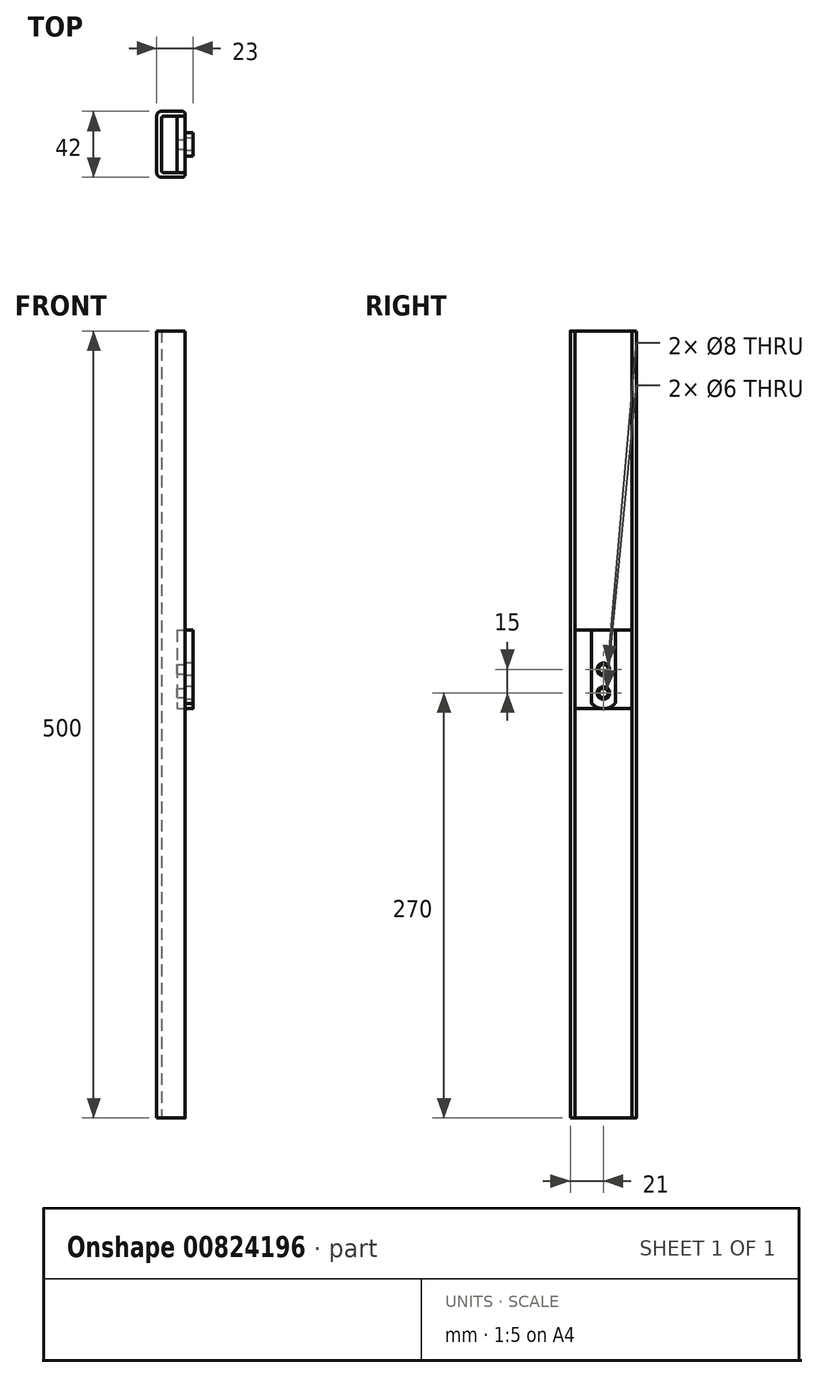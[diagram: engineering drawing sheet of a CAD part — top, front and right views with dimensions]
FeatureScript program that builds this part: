
annotation { "Feature Type Name" : "Feature", "Feature Type Description" : "" }
export const myFeature = defineFeature(function(context is Context, id is Id, definition is map)
    precondition{}
    {
        {
            var Q0;
            Q0=qCreatedBy(makeId("Top.planeOp"),FACE);
            var sketch = newSketch(context, id + "F0", { "sketchPlane" : qUnion([Q0])});
            skLineSegment(sketch, "E0.bottom", {"start": v(7, 21) * mm, "end": v(-6, 21) * mm});
            skLineSegment(sketch, "E0.top", {"start": v(7, -21) * mm, "end": v(-6, -21) * mm});
            skLineSegment(sketch, "E0.left", {"start": v(9, 19) * mm, "end": v(9, -19) * mm});
            skLineSegment(sketch, "E0.right", {"start": v(-9, 18) * mm, "end": v(-9, -18) * mm});
            skPoint(sketch, "E0.middle", {"position": v(0, 0) * mm});
            skLineSegment(sketch, "E1.0", {"start": v(9, -18) * mm, "end": v(-4.5, -18) * mm});
            skLineSegment(sketch, "E1.1", {"start": v(-6, 16.5) * mm, "end": v(-6, -16.5) * mm});
            skLineSegment(sketch, "E1.2", {"start": v(9, 18) * mm, "end": v(-4.5, 18) * mm});
            skPoint(sketch, "E2.visualSharp", {"position": v(-6, 18) * mm});
            skArc(sketch, "E2.filletArc", {"start": v(-4.5, 18) * mm, "mid": v(-5.56, 17.56) * mm, "end": v(-6, 16.5) * mm});
            skPoint(sketch, "E3.visualSharp", {"position": v(-6, -18) * mm});
            skArc(sketch, "E3.filletArc", {"start": v(-6, -16.5) * mm, "mid": v(-5.56, -17.56) * mm, "end": v(-4.5, -18) * mm});
            skPoint(sketch, "E4.visualSharp", {"position": v(-9, -21) * mm});
            skArc(sketch, "E4.filletArc", {"start": v(-9, -18) * mm, "mid": v(-8.12, -20.12) * mm, "end": v(-6, -21) * mm});
            skPoint(sketch, "E5.visualSharp", {"position": v(-9, 21) * mm});
            skArc(sketch, "E5.filletArc", {"start": v(-6, 21) * mm, "mid": v(-8.12, 20.12) * mm, "end": v(-9, 18) * mm});
            skPoint(sketch, "E6.visualSharp", {"position": v(9, -21) * mm});
            skArc(sketch, "E6.filletArc", {"start": v(7, -21) * mm, "mid": v(8.41, -20.41) * mm, "end": v(9, -19) * mm});
            skPoint(sketch, "E7.visualSharp", {"position": v(9, 21) * mm});
            skArc(sketch, "E7.filletArc", {"start": v(9, 19) * mm, "mid": v(8.41, 20.41) * mm, "end": v(7, 21) * mm});
            skSolve(sketch);
        }
        {
            var Q0;
            {var subQ2=sQuery(id+"F0.wireOp",EDGE,"E0.bottom");Q0=makeQuery(id+"F0.imprint","IMPRINT",FACE,{"disambiguationData":[TD([[makeQuery(id+"F0.imprint","IMPRINT",EDGE,{"derivedFrom":subQ2}),1.0]])]});}
            extrude(context, id + "F1", {"entities" : qUnion([Q0]), "depth" : 500 * mm, "offsetDistance" : 25 * mm});
        }
        {
            var Q0;
            {var subQ0=sQuery(id+"F0.wireOp",EDGE,"E0.left");Q0=makeQuery(id+"F1.opExtrude","SWEPT_FACE",FACE,{"disambiguationData":[OSD([subQ0]),TDD([makeQuery(id+"F0.imprint","IMPRINT",EDGE,{"disambiguationData":[TD([[makeQuery(id+"F0.imprint","INTERSECT",VERTEX,{"derivedFrom":[subQ0,sQuery(id+"F0.wireOp",EDGE,"E6.filletArc")]}),1.0]])],"derivedFrom":subQ0})])]});}
            var sketch = newSketch(context, id + "F2", { "sketchPlane" : qUnion([Q0])});
            skLineSegment(sketch, "E8.0.0", {"start": v(18, 0) * mm, "end": v(19, 0) * mm});
            skLineSegment(sketch, "E8.0.1", {"start": v(19, 0) * mm, "end": v(19, 500) * mm});
            skLineSegment(sketch, "E8.0.2", {"start": v(19, 500) * mm, "end": v(18, 500) * mm});
            skLineSegment(sketch, "E8.0.3", {"start": v(18, 500) * mm, "end": v(18, 0) * mm});
            skLineSegment(sketch, "E9.bottom", {"start": v(-18, 260) * mm, "end": v(18, 260) * mm});
            skLineSegment(sketch, "E9.top", {"start": v(-18, 310) * mm, "end": v(18, 310) * mm});
            skLineSegment(sketch, "E9.left", {"start": v(-18, 260) * mm, "end": v(-18, 310) * mm});
            skLineSegment(sketch, "E9.right", {"start": v(18, 260) * mm, "end": v(18, 310) * mm});
            skLineSegment(sketch, "E10", {"start": v(0, 310) * mm, "end": v(0, 260) * mm, "construction": true});
            skPoint(sketch, "E11", {"position": v(0, 270) * mm});
            skPoint(sketch, "E12", {"position": v(0, 285) * mm});
            skCircle(sketch, "E13", {"center": v(0, 270) * mm, "radius": 3 * mm});
            skCircle(sketch, "E14", {"center": v(0, 285) * mm, "radius": 3 * mm});
            skSolve(sketch);
        }
        {
            var Q0;
            Q0=makeQuery(id+"F2.imprint","IMPRINT",FACE,{"disambiguationData":[TD([[makeQuery(id+"F2.imprint","IMPRINT",EDGE,{"derivedFrom":sQuery(id+"F2.wireOp",EDGE,"E9.bottom")}),1.0]])]});
            extrude(context, id + "F3", {"entities" : qUnion([Q0]), "oppositeDirection" : true, "depth" : 5 * mm, "offsetDistance" : 25 * mm});
        }
        {
            var Q0;
            Q0=makeQuery(id+"F3.opExtrude","CAP_FACE",FACE,{"disambiguationData":[OSD([sQuery(id+"F2.wireOp",EDGE,"E9.bottom"),sQuery(id+"F2.wireOp",EDGE,"E9.top"),sQuery(id+"F2.wireOp",EDGE,"E9.left"),sQuery(id+"F2.wireOp",EDGE,"E9.right"),sQuery(id+"F2.wireOp",EDGE,"E13"),sQuery(id+"F2.wireOp",EDGE,"E14")])],"isStart":true});
            var sketch = newSketch(context, id + "F4", { "sketchPlane" : qUnion([Q0])});
            skLineSegment(sketch, "E15.top", {"start": v(-7.5, 310) * mm, "end": v(7.5, 310) * mm});
            skLineSegment(sketch, "E15.left", {"start": v(-7.5, 263.39) * mm, "end": v(-7.5, 310) * mm});
            skLineSegment(sketch, "E15.right", {"start": v(7.5, 263.39) * mm, "end": v(7.5, 310) * mm});
            skCircle(sketch, "E16.0", {"center": v(0, 285) * mm, "radius": 3 * mm});
            skCircle(sketch, "E17.0", {"center": v(0, 270) * mm, "radius": 3 * mm});
            skArc(sketch, "E18", {"start": v(-7.5, 263.39) * mm, "mid": v(0, 260) * mm, "end": v(7.5, 263.39) * mm});
            skPoint(sketch, "E19.orphan", {"position": v(-7.5, 260) * mm});
            skPoint(sketch, "E20.orphan", {"position": v(7.5, 260) * mm});
            skCircle(sketch, "E21", {"center": v(0, 270) * mm, "radius": 4 * mm});
            skCircle(sketch, "E22", {"center": v(0, 285) * mm, "radius": 4 * mm});
            skSolve(sketch);
        }
        {
            var Q0;
            Q0 = qSketchRegion(id + "F4", true);
            extrude(context, id + "F5", {"entities" : qUnion([Q0]), "depth" : 5 * mm, "offsetDistance" : 25 * mm});
        }
    });
